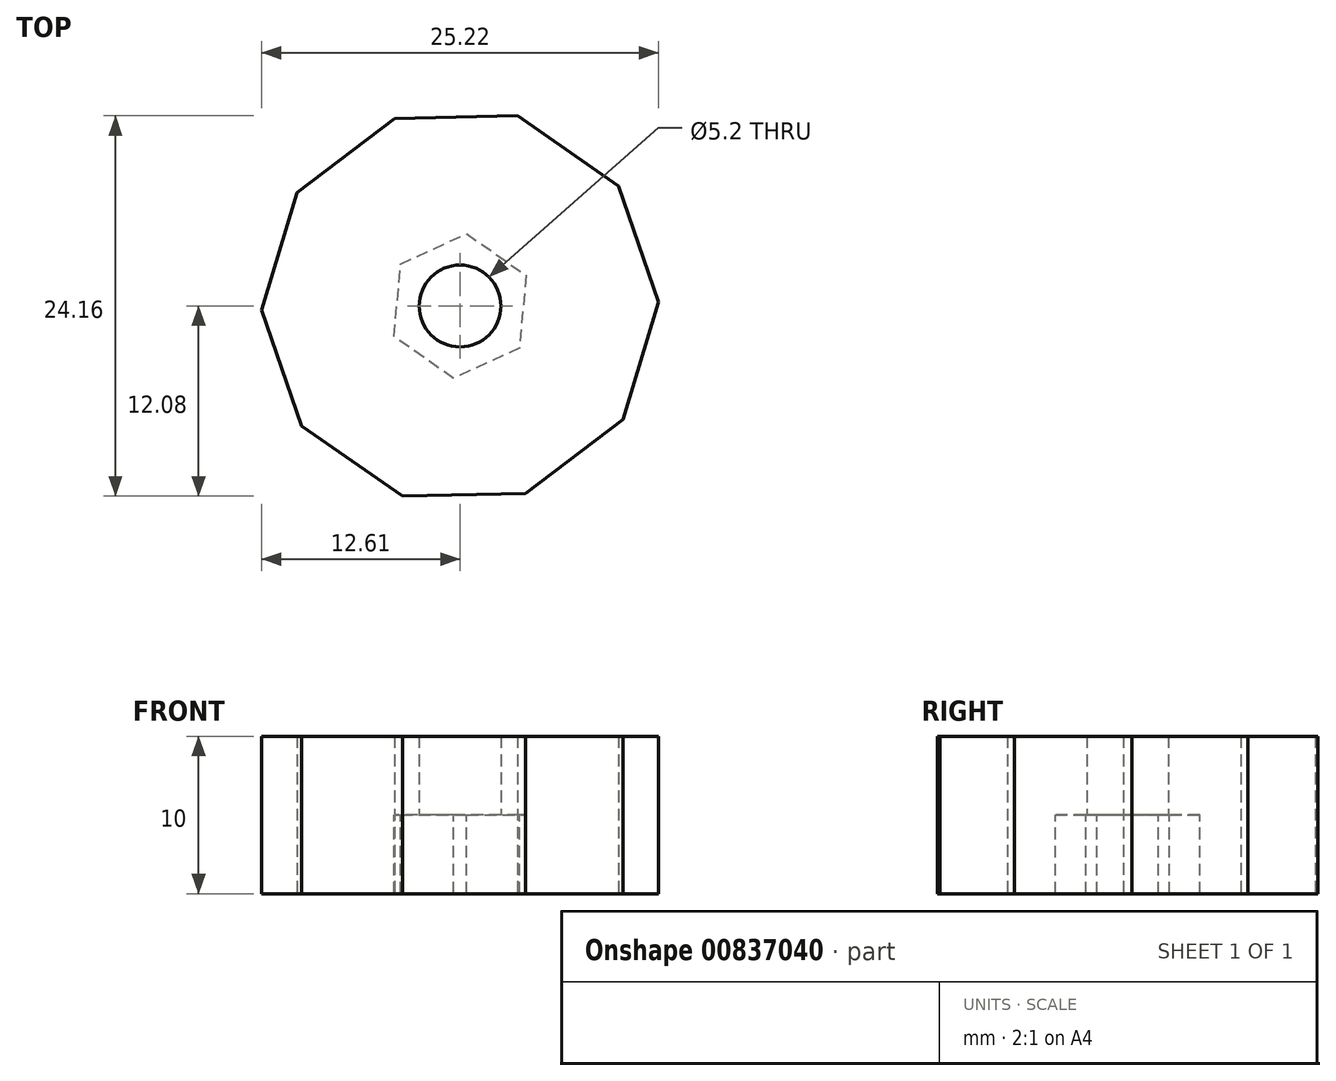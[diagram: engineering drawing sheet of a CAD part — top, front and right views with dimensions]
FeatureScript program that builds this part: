
annotation { "Feature Type Name" : "Feature", "Feature Type Description" : "" }
export const myFeature = defineFeature(function(context is Context, id is Id, definition is map)
    precondition{}
    {
        {
            var Q0;
            Q0=qCreatedBy(makeId("Top.planeOp"),FACE);
            var sketch = newSketch(context, id + "F0", { "sketchPlane" : qUnion([Q0])});
            skCircle(sketch, "E0", {"center": v(0, 0) * mm, "radius": 12 * mm});
            skCircle(sketch, "E1", {"center": v(0, 0) * mm, "radius": 2.6 * mm});
            skCircle(sketch, "E2.cCircle", {"center": v(0, 0) * mm, "radius": 12 * mm, "construction": true});
            skLineSegment(sketch, "E2.0", {"start": v(-10.36, 7.2) * mm, "end": v(-4.15, 11.92) * mm});
            skLineSegment(sketch, "E2.1", {"start": v(-4.15, 11.92) * mm, "end": v(3.65, 12.08) * mm});
            skLineSegment(sketch, "E2.2", {"start": v(3.65, 12.08) * mm, "end": v(10.05, 7.63) * mm});
            skLineSegment(sketch, "E2.3", {"start": v(10.05, 7.63) * mm, "end": v(12.61, 0.26) * mm});
            skLineSegment(sketch, "E2.4", {"start": v(12.61, 0.26) * mm, "end": v(10.36, -7.2) * mm});
            skLineSegment(sketch, "E2.5", {"start": v(10.36, -7.2) * mm, "end": v(4.15, -11.92) * mm});
            skLineSegment(sketch, "E2.6", {"start": v(4.15, -11.92) * mm, "end": v(-3.65, -12.08) * mm});
            skLineSegment(sketch, "E2.7", {"start": v(-3.65, -12.08) * mm, "end": v(-10.05, -7.63) * mm});
            skLineSegment(sketch, "E2.8", {"start": v(-10.05, -7.63) * mm, "end": v(-12.61, -0.26) * mm});
            skLineSegment(sketch, "E2.9", {"start": v(-12.61, -0.26) * mm, "end": v(-10.36, 7.2) * mm});
            skPoint(sketch, "E2.0.midPoint", {"position": v(-7.25, 9.56) * mm});
            skSolve(sketch);
        }
        {
            var Q0;
            Q0=makeQuery(id+"F0.imprint","IMPRINT",FACE,{"disambiguationData":[TD([[makeQuery(id+"F0.imprint","IMPRINT",EDGE,{"derivedFrom":sQuery(id+"F0.wireOp",EDGE,"E0")}),1.0]])]});
            var Q1;
            {var subQ0=sQuery(id+"F0.wireOp",EDGE,"E2.9");var subQ1=sQuery(id+"F0.wireOp",EDGE,"E0");var subQ2=makeQuery(id+"F0.imprint","INTERSECT",VERTEX,{"derivedFrom":[subQ1,subQ0]});Q1=makeQuery(id+"F0.imprint","IMPRINT",FACE,{"disambiguationData":[TD([[makeQuery(id+"F0.imprint","IMPRINT",EDGE,{"disambiguationData":[TD([[subQ2,-1.0]])],"derivedFrom":subQ1}),-1.0]])]});}
            var Q2;
            {var subQ0=sQuery(id+"F0.wireOp",EDGE,"E2.0");var subQ1=sQuery(id+"F0.wireOp",EDGE,"E0");var subQ2=makeQuery(id+"F0.imprint","INTERSECT",VERTEX,{"derivedFrom":[subQ1,subQ0]});Q2=makeQuery(id+"F0.imprint","IMPRINT",FACE,{"disambiguationData":[TD([[makeQuery(id+"F0.imprint","IMPRINT",EDGE,{"disambiguationData":[TD([[subQ2,-1.0]])],"derivedFrom":subQ1}),-1.0]])]});}
            var Q3;
            {var subQ0=sQuery(id+"F0.wireOp",EDGE,"E2.2");var subQ1=sQuery(id+"F0.wireOp",EDGE,"E0");var subQ2=makeQuery(id+"F0.imprint","INTERSECT",VERTEX,{"derivedFrom":[subQ1,subQ0]});Q3=makeQuery(id+"F0.imprint","IMPRINT",FACE,{"disambiguationData":[TD([[makeQuery(id+"F0.imprint","IMPRINT",EDGE,{"disambiguationData":[TD([[subQ2,-1.0]])],"derivedFrom":subQ1}),-1.0]])]});}
            var Q4;
            {var subQ0=sQuery(id+"F0.wireOp",EDGE,"E2.1");var subQ1=sQuery(id+"F0.wireOp",EDGE,"E0");var subQ2=makeQuery(id+"F0.imprint","INTERSECT",VERTEX,{"derivedFrom":[subQ1,subQ0]});Q4=makeQuery(id+"F0.imprint","IMPRINT",FACE,{"disambiguationData":[TD([[makeQuery(id+"F0.imprint","IMPRINT",EDGE,{"disambiguationData":[TD([[subQ2,-1.0]])],"derivedFrom":subQ1}),-1.0]])]});}
            var Q5;
            {var subQ0=sQuery(id+"F0.wireOp",EDGE,"E2.3");var subQ1=sQuery(id+"F0.wireOp",EDGE,"E0");var subQ2=makeQuery(id+"F0.imprint","INTERSECT",VERTEX,{"derivedFrom":[subQ1,subQ0]});Q5=makeQuery(id+"F0.imprint","IMPRINT",FACE,{"disambiguationData":[TD([[makeQuery(id+"F0.imprint","IMPRINT",EDGE,{"disambiguationData":[TD([[subQ2,1.0]])],"derivedFrom":subQ1}),-1.0]])]});}
            var Q6;
            {var subQ0=sQuery(id+"F0.wireOp",EDGE,"E2.5");var subQ1=sQuery(id+"F0.wireOp",EDGE,"E0");var subQ2=makeQuery(id+"F0.imprint","INTERSECT",VERTEX,{"derivedFrom":[subQ1,subQ0]});Q6=makeQuery(id+"F0.imprint","IMPRINT",FACE,{"disambiguationData":[TD([[makeQuery(id+"F0.imprint","IMPRINT",EDGE,{"disambiguationData":[TD([[subQ2,-1.0]])],"derivedFrom":subQ1}),-1.0]])]});}
            var Q7;
            {var subQ0=sQuery(id+"F0.wireOp",EDGE,"E2.6");var subQ1=sQuery(id+"F0.wireOp",EDGE,"E0");var subQ2=makeQuery(id+"F0.imprint","INTERSECT",VERTEX,{"derivedFrom":[subQ1,subQ0]});Q7=makeQuery(id+"F0.imprint","IMPRINT",FACE,{"disambiguationData":[TD([[makeQuery(id+"F0.imprint","IMPRINT",EDGE,{"disambiguationData":[TD([[subQ2,-1.0]])],"derivedFrom":subQ1}),-1.0]])]});}
            var Q8;
            {var subQ0=sQuery(id+"F0.wireOp",EDGE,"E2.7");var subQ1=sQuery(id+"F0.wireOp",EDGE,"E0");var subQ2=makeQuery(id+"F0.imprint","INTERSECT",VERTEX,{"derivedFrom":[subQ1,subQ0]});Q8=makeQuery(id+"F0.imprint","IMPRINT",FACE,{"disambiguationData":[TD([[makeQuery(id+"F0.imprint","IMPRINT",EDGE,{"disambiguationData":[TD([[subQ2,-1.0]])],"derivedFrom":subQ1}),-1.0]])]});}
            var Q9;
            {var subQ0=sQuery(id+"F0.wireOp",EDGE,"E2.2");var subQ1=sQuery(id+"F0.wireOp",EDGE,"E0");var subQ2=makeQuery(id+"F0.imprint","INTERSECT",VERTEX,{"derivedFrom":[subQ1,subQ0]});Q9=makeQuery(id+"F0.imprint","IMPRINT",FACE,{"disambiguationData":[TD([[makeQuery(id+"F0.imprint","IMPRINT",EDGE,{"disambiguationData":[TD([[subQ2,1.0]])],"derivedFrom":subQ1}),-1.0]])]});}
            var Q10;
            {var subQ0=sQuery(id+"F0.wireOp",EDGE,"E2.8");var subQ1=sQuery(id+"F0.wireOp",EDGE,"E0");var subQ2=makeQuery(id+"F0.imprint","INTERSECT",VERTEX,{"derivedFrom":[subQ1,subQ0]});Q10=makeQuery(id+"F0.imprint","IMPRINT",FACE,{"disambiguationData":[TD([[makeQuery(id+"F0.imprint","IMPRINT",EDGE,{"disambiguationData":[TD([[subQ2,-1.0]])],"derivedFrom":subQ1}),-1.0]])]});}
            extrude(context, id + "F1", {"entities" : qUnion([Q0, Q1, Q2, Q3, Q4, Q5, Q6, Q7, Q8, Q9, Q10]), "depth" : 10 * mm, "offsetDistance" : 25 * mm});
        }
        {
            var Q0;
            Q0=qCreatedBy(makeId("Top.planeOp"),FACE);
            var sketch = newSketch(context, id + "F2", { "sketchPlane" : qUnion([Q0])});
            skCircle(sketch, "E3.cCircle", {"center": v(0, 0) * mm, "radius": 4 * mm, "construction": true});
            skLineSegment(sketch, "E3.0", {"start": v(-3.78, 2.66) * mm, "end": v(0.41, 4.6) * mm});
            skLineSegment(sketch, "E3.1", {"start": v(0.41, 4.6) * mm, "end": v(4.2, 1.94) * mm});
            skLineSegment(sketch, "E3.2", {"start": v(4.2, 1.94) * mm, "end": v(3.78, -2.66) * mm});
            skLineSegment(sketch, "E3.3", {"start": v(3.78, -2.66) * mm, "end": v(-0.41, -4.6) * mm});
            skLineSegment(sketch, "E3.4", {"start": v(-0.41, -4.6) * mm, "end": v(-4.2, -1.94) * mm});
            skLineSegment(sketch, "E3.5", {"start": v(-4.2, -1.94) * mm, "end": v(-3.78, 2.66) * mm});
            skPoint(sketch, "E3.0.midPoint", {"position": v(-1.68, 3.63) * mm});
            skSolve(sketch);
        }
        {
            var Q0;
            Q0=makeQuery(id+"F2.imprint","IMPRINT",FACE,{"disambiguationData":[TD([[makeQuery(id+"F2.imprint","IMPRINT",EDGE,{"derivedFrom":sQuery(id+"F2.wireOp",EDGE,"E3.0")}),-1.0]])]});
            extrude(context, id + "F3", {"entities" : qUnion([Q0]), "operationType" : NewBodyOperationType.REMOVE, "oppositeDirection" : true, "depth" : 10 * mm, "offsetDistance" : 25 * mm, "hasSecondDirection" : true, "secondDirectionOppositeDirection" : false, "secondDirectionDepth" : 5 * mm});
        }
    });
